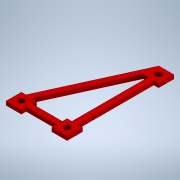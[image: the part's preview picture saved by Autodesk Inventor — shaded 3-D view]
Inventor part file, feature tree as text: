
AUTODESK INVENTOR PART (.ipt)
format: ipt  version: 2020 (Build 240168000, 168)  size: 158,720 bytes
history: native  units: mm
features: sketch x2, other x1, extrude x1
ambient origin geometry x8: Origin, YZ Plane, XZ Plane, XY Plane, X Axis, Y Axis, Z Axis, Center Point
bodies: Solid1 (feature_tree)
feature tree (4):
  other  "HexBodyV2.ipt"
  extrude  "Extrusion1"  Depth=10.0mm
  sketch  "Sketch14"  dims[d2=3.1mm d3=3.1mm d4=3.0mm d5=3.0mm d6=3.0mm d7=2.0mm d8=0.0mm]
  sketch  "Sketch2"  dims[d0=10.0mm d1=3.1mm]
